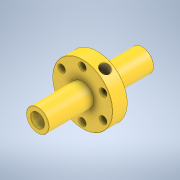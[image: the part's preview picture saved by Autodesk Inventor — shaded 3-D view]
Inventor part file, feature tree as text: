
AUTODESK INVENTOR PART (.ipt)
format: ipt  version: 2020 (Build 240168000, 168)  size: 178,176 bytes
history: native  units: mm
features: sketch x3, hole x2, plane x2, revolve x1, pattern_circular x1, chamfer x1
ambient origin geometry x8: Origin, YZ Plane, XZ Plane, XY Plane, X Axis, Y Axis, Z Axis, Center Point
bodies: Solid1 (feature_tree)
feature tree (10):
  revolve  "Revolution1"  [1 undecoded]
  hole  "Hole1"  [1 undecoded]
  pattern_circular  "Circular Pattern1"  Count=4  [1 undecoded]
  plane  "Work Plane2"
  hole  "Hole2"  [1 undecoded]
  chamfer  "Chamfer1"  Distance=60.0mm Angle=360.0deg
  sketch  "Sketch1"  dims[d0=9.0mm d1=15.0mm]
  sketch  "Sketch2"  dims[d2=30.0mm d3=10.0mm d4=40.0mm]
  plane  "Work Plane1"
  sketch  "Sketch3"  dims[d5=90.0deg d6=16.0mm d7=5.0mm d8=6.0mm d9=4.0mm d10=2.0mm d11=90.0deg d12=8.0mm d13=20.594885mm d14=60.0mm d15=360.0deg d17=60.0deg d18=6.647mm d19=10.0mm d20=4.0mm d21=2.0mm d22=90.0deg d23=20.2mm d24=20.594885mm d25=0.2mm d26=2.0mm d27=45.0deg d28=30.0mm]
note: 4 required parameter values undecoded (feature->parameter linkage not recoverable at this tier; creation-order binding heuristic only, values carry confidence <= 0.55)